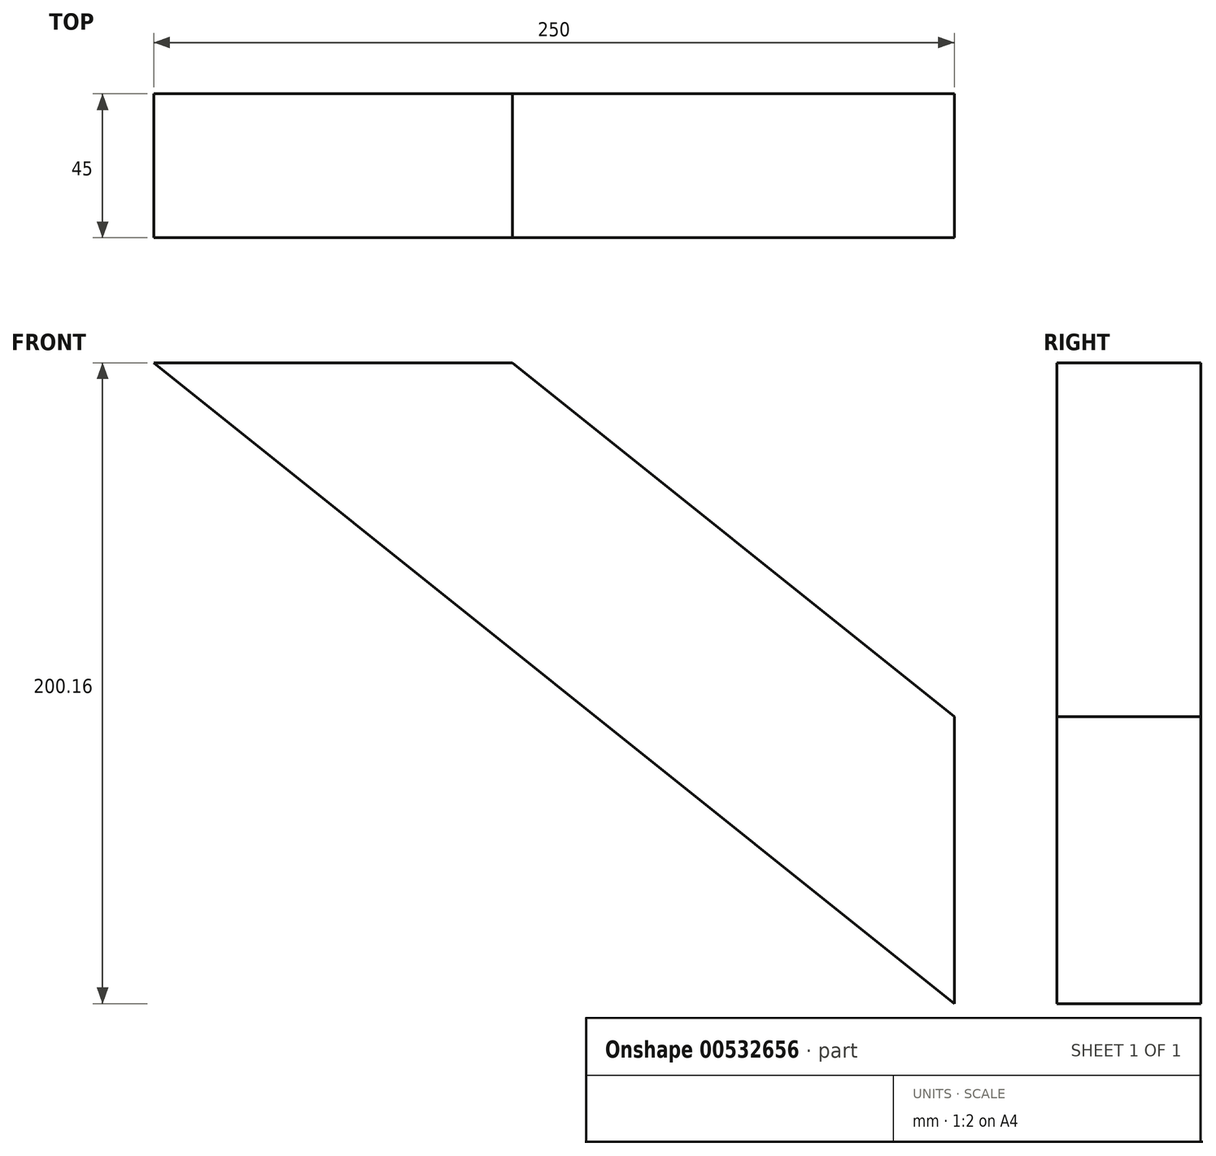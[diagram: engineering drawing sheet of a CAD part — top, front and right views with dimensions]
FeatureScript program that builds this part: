
annotation { "Feature Type Name" : "Feature", "Feature Type Description" : "" }
export const myFeature = defineFeature(function(context is Context, id is Id, definition is map)
    precondition{}
    {
        {
            var Q0;
            Q0=qCreatedBy(makeId("Front.planeOp"),FACE);
            var sketch = newSketch(context, id + "F0", { "sketchPlane" : qUnion([Q0])});
            skLineSegment(sketch, "E0", {"start": v(-41, 77.66) * mm, "end": v(97, -32.83) * mm});
            skLineSegment(sketch, "E1", {"start": v(-153, 77.66) * mm, "end": v(97, -122.5) * mm});
            skLineSegment(sketch, "E2", {"start": v(-153, 77.66) * mm, "end": v(-41, 77.66) * mm});
            skLineSegment(sketch, "E3", {"start": v(97, -32.83) * mm, "end": v(97, -122.5) * mm});
            skSolve(sketch);
        }
        {
            var Q0;
            Q0 = qSketchRegion(id + "F0", true);
            extrude(context, id + "F1", {"entities" : qUnion([Q0]), "depth" : 45 * mm, "offsetDistance" : 25 * mm});
        }
    });
